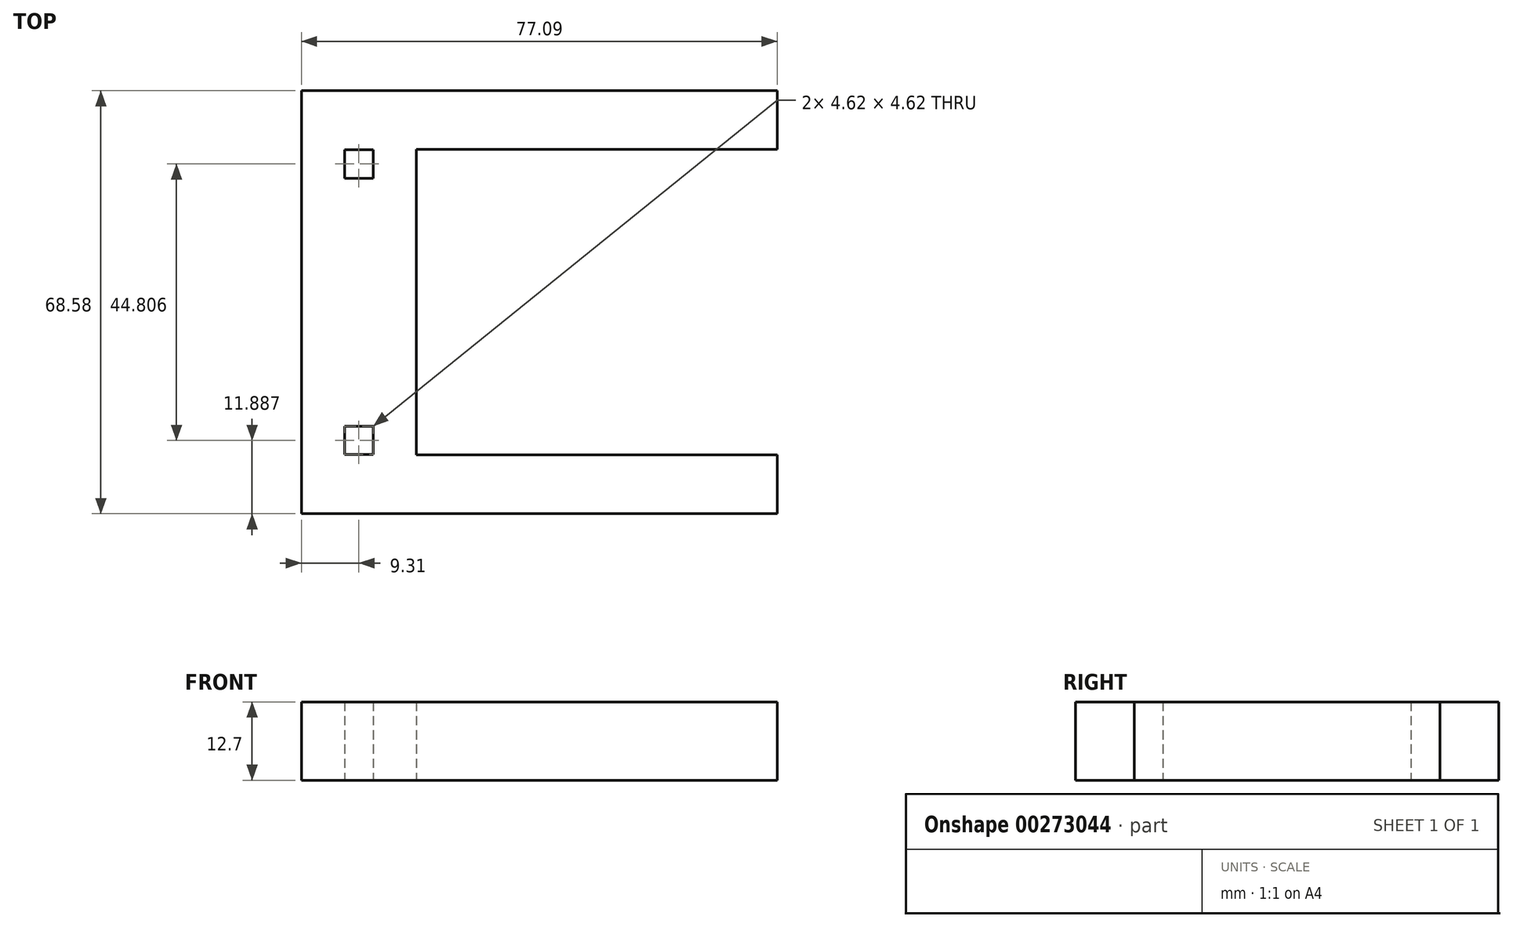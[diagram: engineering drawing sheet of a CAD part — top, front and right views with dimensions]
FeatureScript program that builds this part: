
annotation { "Feature Type Name" : "Feature", "Feature Type Description" : "" }
export const myFeature = defineFeature(function(context is Context, id is Id, definition is map)
    precondition{}
    {
        {
            var Q0;
            Q0=qCreatedBy(makeId("Top.planeOp"),FACE);
            var sketch = newSketch(context, id + "F0", { "sketchPlane" : qUnion([Q0])});
            skLineSegment(sketch, "E0.bottom", {"start": v(-9.31, 34.3) * mm, "end": v(9.31, 34.3) * mm});
            skLineSegment(sketch, "E0.top", {"start": v(-9.31, -34.3) * mm, "end": v(9.31, -34.3) * mm});
            skLineSegment(sketch, "E0.left", {"start": v(-9.31, 34.3) * mm, "end": v(-9.31, -34.3) * mm});
            skLineSegment(sketch, "E0.right", {"start": v(9.31, 34.3) * mm, "end": v(9.31, -34.3) * mm});
            skPoint(sketch, "E0.middle", {"position": v(0, 0) * mm});
            skLineSegment(sketch, "E1.bottom", {"start": v(9.31, 34.3) * mm, "end": v(67.78, 34.3) * mm});
            skLineSegment(sketch, "E1.top", {"start": v(9.31, 24.77) * mm, "end": v(67.78, 24.77) * mm});
            skLineSegment(sketch, "E1.left", {"start": v(9.31, 34.3) * mm, "end": v(9.31, 24.77) * mm});
            skLineSegment(sketch, "E1.right", {"start": v(67.78, 34.3) * mm, "end": v(67.78, 24.77) * mm});
            skPoint(sketch, "E2.endSnap0", {"position": v(9.31, 0) * mm});
            skLineSegment(sketch, "E3.MirrorCS", {"start": v(67.78, -34.29) * mm, "end": v(67.78, -24.76) * mm});
            skLineSegment(sketch, "E4.MirrorCS", {"start": v(9.31, -24.77) * mm, "end": v(67.78, -24.76) * mm});
            skLineSegment(sketch, "E5.MirrorCS", {"start": v(9.31, -34.3) * mm, "end": v(67.78, -34.29) * mm});
            skLineSegment(sketch, "E6.bottom", {"start": v(-2.31, 24.71) * mm, "end": v(2.31, 24.71) * mm});
            skLineSegment(sketch, "E6.top", {"start": v(-2.31, 20.1) * mm, "end": v(2.31, 20.1) * mm});
            skLineSegment(sketch, "E6.left", {"start": v(-2.31, 24.71) * mm, "end": v(-2.31, 20.1) * mm});
            skLineSegment(sketch, "E6.right", {"start": v(2.31, 24.71) * mm, "end": v(2.31, 20.1) * mm});
            skPoint(sketch, "E6.middle", {"position": v(0, 22.4) * mm});
            skLineSegment(sketch, "E7", {"start": v(0, 0) * mm, "end": v(31.27, 0) * mm});
            skLineSegment(sketch, "E8.MirrorCS", {"start": v(-2.31, -20.1) * mm, "end": v(2.31, -20.1) * mm});
            skLineSegment(sketch, "E9.MirrorCS", {"start": v(2.31, -24.71) * mm, "end": v(2.31, -20.1) * mm});
            skLineSegment(sketch, "E10.MirrorCS", {"start": v(-2.31, -24.71) * mm, "end": v(-2.31, -20.1) * mm});
            skLineSegment(sketch, "E11.MirrorCS", {"start": v(-2.31, -24.71) * mm, "end": v(2.31, -24.71) * mm});
            skSolve(sketch);
        }
        {
            var Q0;
            Q0=makeQuery(id+"F0.imprint","IMPRINT",FACE,{"disambiguationData":[TD([[makeQuery(id+"F0.imprint","IMPRINT",EDGE,{"derivedFrom":sQuery(id+"F0.wireOp",EDGE,"E0.bottom")}),-1.0]])]});
            var Q1;
            Q1=makeQuery(id+"F0.imprint","IMPRINT",FACE,{"disambiguationData":[TD([[makeQuery(id+"F0.imprint","IMPRINT",EDGE,{"derivedFrom":sQuery(id+"F0.wireOp",EDGE,"E1.bottom")}),-1.0]])]});
            var Q2;
            Q2=makeQuery(id+"F0.imprint","IMPRINT",FACE,{"disambiguationData":[TD([[makeQuery(id+"F0.imprint","IMPRINT",EDGE,{"derivedFrom":sQuery(id+"F0.wireOp",EDGE,"E3.MirrorCS")}),1.0]])]});
            extrude(context, id + "F1", {"entities" : qUnion([Q0, Q1, Q2]), "depth" : 12.7 * mm});
        }
    });
